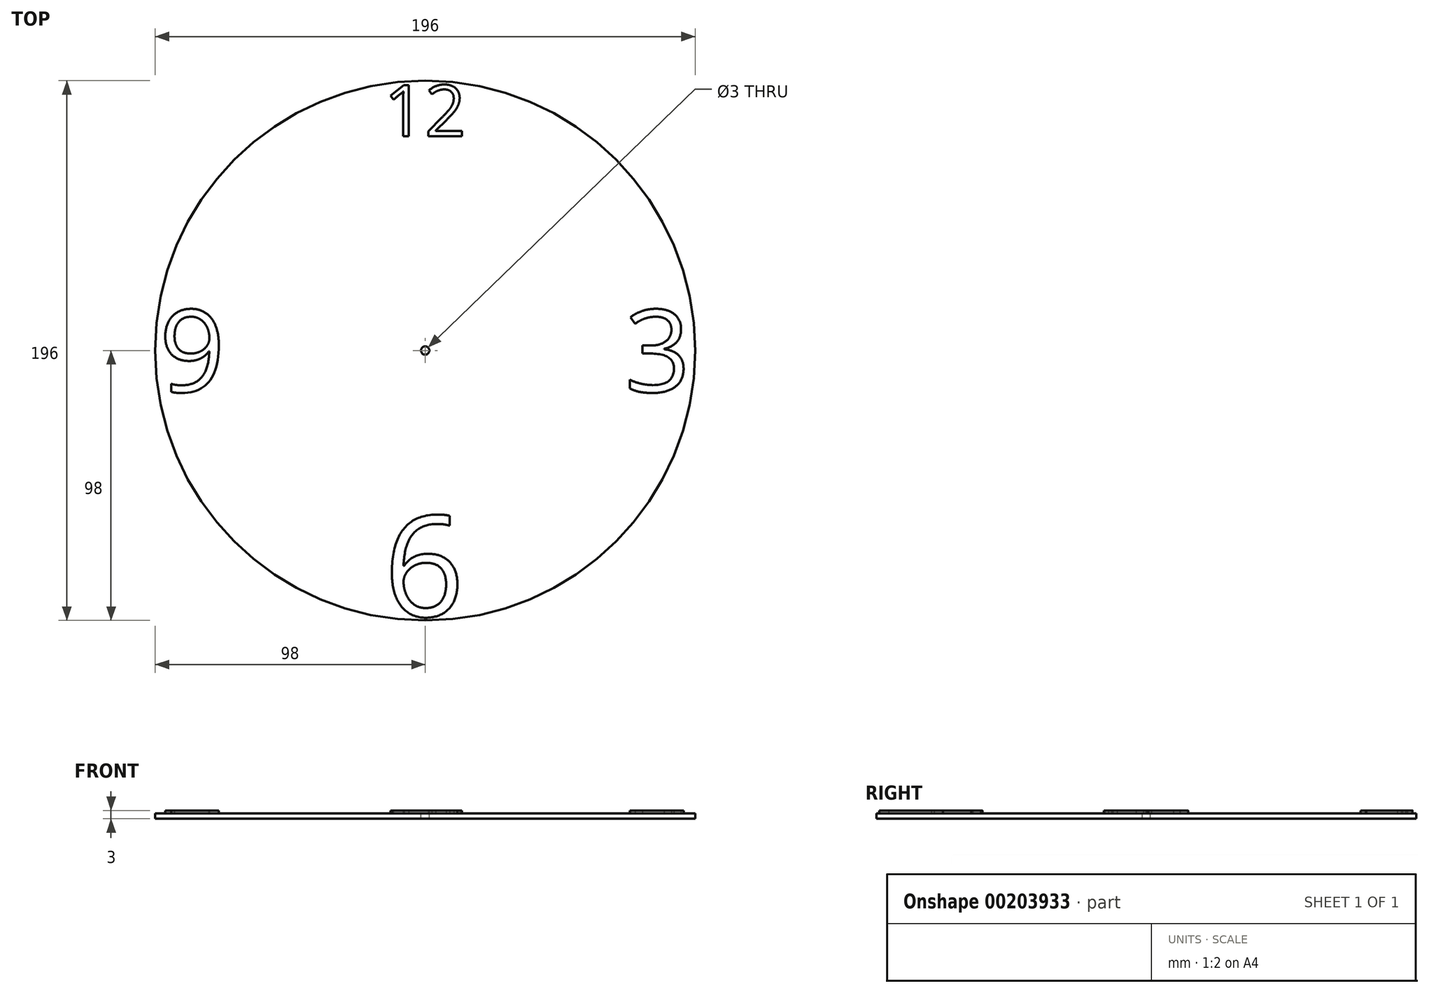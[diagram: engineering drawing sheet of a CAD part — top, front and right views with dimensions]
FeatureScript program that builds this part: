
annotation { "Feature Type Name" : "Feature", "Feature Type Description" : "" }
export const myFeature = defineFeature(function(context is Context, id is Id, definition is map)
    precondition{}
    {
        {
            var Q0;
            Q0=qCreatedBy(makeId("Top.planeOp"),FACE);
            var sketch = newSketch(context, id + "F0", { "sketchPlane" : qUnion([Q0])});
            skCircle(sketch, "E0", {"center": v(0, 0) * mm, "radius": 98 * mm});
            skSolve(sketch);
        }
        {
            var Q0;
            Q0=qSketchRegion(id+"F0",true);
            extrude(context, id + "F1", {"entities" : qUnion([Q0]), "depth" : 2 * mm});
        }
        {
            var Q0;
            Q0=makeQuery(id+"F1.opExtrude","CAP_FACE",FACE,{"disambiguationData":[OSD([sQuery(id+"F0.wireOp",EDGE,"E0")])],"isStart":false});
            var sketch = newSketch(context, id + "F2", { "sketchPlane" : qUnion([Q0])});
            skText(sketch, "E1", { "text": "12\n", "fontName": "OpenSans-Regular.ttf"});
            skText(sketch, "E2", { "text": "6", "fontName": "OpenSans-Regular.ttf"});
            skText(sketch, "E3", { "text": "3", "fontName": "OpenSans-Regular.ttf"});
            skLineSegment(sketch, "E4", {"start": v(95, 0) * mm, "end": v(70.92, 0) * mm, "construction": true});
            skText(sketch, "E5", { "text": "9", "fontName": "OpenSans-Regular.ttf"});
            skLineSegment(sketch, "E6", {"start": v(-70.7, 0) * mm, "end": v(-95, 0) * mm, "construction": true});
            const initialGuessF2  = {"E1": [-0.015, 0.0778, 1, 0, 0.0187], "E2": [-0.015, -0.0965, 1, 0, 0.03675], "E3": [0.07242, -0.015, 1, 0, 0.03], "E5": [-0.0965, -0.015, 1, 0, 0.03]};
            skSetInitialGuess(sketch, initialGuessF2);
            skSolve(sketch);
        }
        {
            var Q0;
            Q0=qSketchRegion(id+"F2",true);
            extrude(context, id + "F3", {"entities" : qUnion([Q0]), "operationType" : NewBodyOperationType.ADD, "depth" : 1 * mm});
        }
        {
            var Q0;
            {var subQ0=sQuery(id+"F0.wireOp",EDGE,"E0");Q0=makeQuery(id+"F3.boolean.opBoolean","SPLIT",FACE,{"disambiguationData":[TD([makeQuery(id+"F1.opExtrude","SWEPT_FACE",FACE,{"disambiguationData":[OSD([subQ0])]})])],"derivedFrom":makeQuery(id+"F1.opExtrude","CAP_FACE",FACE,{"disambiguationData":[OSD([subQ0])],"isStart":false})});}
            var sketch = newSketch(context, id + "F4", { "sketchPlane" : qUnion([Q0])});
            skCircle(sketch, "E7", {"center": v(0, 0) * mm, "radius": 1.5 * mm});
            skSolve(sketch);
        }
        {
            var Q0;
            Q0=qSketchRegion(id+"F4",true);
            extrude(context, id + "F5", {"entities" : qUnion([Q0]), "operationType" : NewBodyOperationType.REMOVE, "oppositeDirection" : true, "depth" : 4 * mm});
        }
    });
